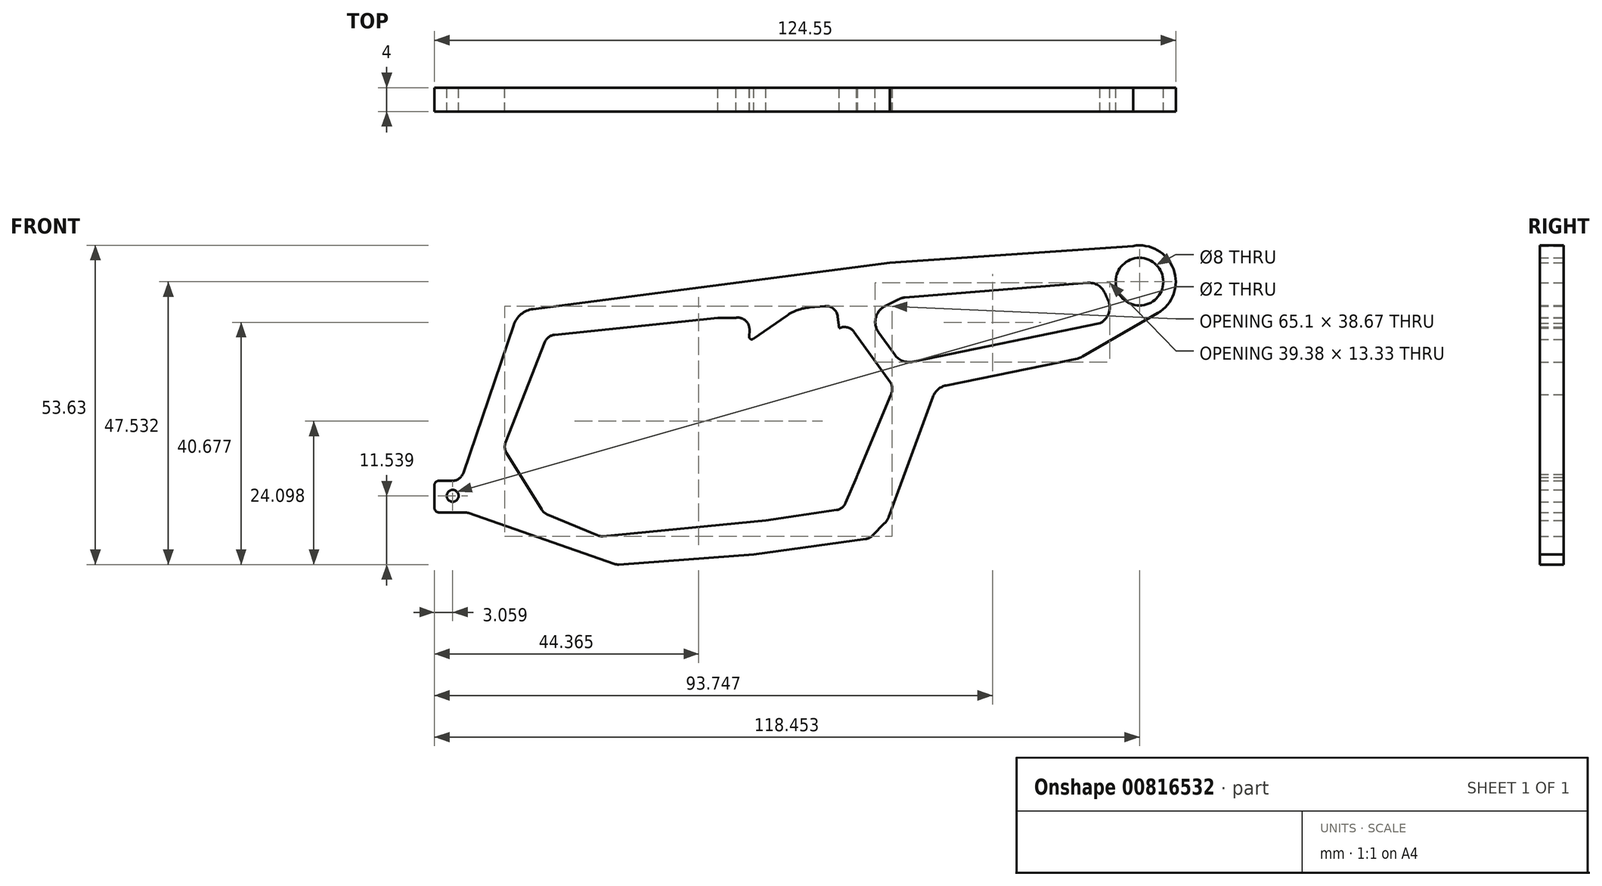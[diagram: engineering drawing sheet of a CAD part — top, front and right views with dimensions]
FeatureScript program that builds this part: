
annotation { "Feature Type Name" : "Feature", "Feature Type Description" : "" }
export const myFeature = defineFeature(function(context is Context, id is Id, definition is map)
    precondition{}
    {
        {
            assignVariable(context, id + "F0", {"name" : "GT_material", "anyValue" : 4});
        }
        {
            var Q0;
            Q0=qCreatedBy(makeId("Front.planeOp"),FACE);
            var sketch = newSketch(context, id + "F1", { "sketchPlane" : qUnion([Q0])});
            skCircle(sketch, "E0", {"center": v(51.04, 1.14) * mm, "radius": 4 * mm});
            skArc(sketch, "E1", {"start": v(-14.48, -6.96) * mm, "mid": v(-15.14, -5.41) * mm, "end": v(-16.75, -4.91) * mm});
            skLineSegment(sketch, "E2", {"start": v(-19.77, -4.91) * mm, "end": v(-16.75, -4.91) * mm});
            skLineSegment(sketch, "E3", {"start": v(-14.48, -6.96) * mm, "end": v(-14.52, -8.15) * mm});
            skLineSegment(sketch, "E4", {"start": v(-13.92, -8.48) * mm, "end": v(-8.2, -4.55) * mm});
            skLineSegment(sketch, "E5", {"start": v(49.97, 7.14) * mm, "end": v(9.1, 4.35) * mm});
            skPoint(sketch, "E6.visualSharp", {"position": v(-14.55, -8.91) * mm});
            skArc(sketch, "E6.filletArc", {"start": v(-14.52, -8.15) * mm, "mid": v(-14.32, -8.5) * mm, "end": v(-13.92, -8.48) * mm});
            skArc(sketch, "E7", {"start": v(54.1, -4.13) * mm, "mid": v(56.77, 3.24) * mm, "end": v(49.97, 7.14) * mm});
            skLineSegment(sketch, "E8", {"start": v(0.36, -4.73) * mm, "end": v(0.57, -6.68) * mm});
            skLineSegment(sketch, "E9", {"start": v(0.57, -6.68) * mm, "end": v(0.67, -6.63) * mm});
            skLineSegment(sketch, "E10", {"start": v(-1.8, -2.96) * mm, "end": v(-4.35, -3.17) * mm});
            skPoint(sketch, "E11.orphan", {"position": v(1.27, -2.7) * mm});
            skArc(sketch, "E12.filletArc", {"start": v(-4.35, -3.17) * mm, "mid": v(-6.36, -3.61) * mm, "end": v(-8.2, -4.55) * mm});
            skPoint(sketch, "E13.visualSharp", {"position": v(0.15, -2.8) * mm});
            skArc(sketch, "E14.filletArc", {"start": v(0.36, -4.73) * mm, "mid": v(-0.36, -3.4) * mm, "end": v(-1.8, -2.96) * mm});
            skArc(sketch, "E15", {"start": v(9.26, -17.84) * mm, "mid": v(9.5, -16.75) * mm, "end": v(9.13, -15.7) * mm});
            skLineSegment(sketch, "E16", {"start": v(3.1, -7.3) * mm, "end": v(9.13, -15.7) * mm});
            skArc(sketch, "E17", {"start": v(3.48, -31.72) * mm, "mid": v(3.6, -31.5) * mm, "end": v(3.67, -31.26) * mm});
            skLineSegment(sketch, "E18", {"start": v(9.42, -17.45) * mm, "end": v(3.48, -31.72) * mm});
            skLineSegment(sketch, "E19", {"start": v(4.56, -29.14) * mm, "end": v(1.69, -36.02) * mm});
            skPoint(sketch, "E19.endSnap0", {"position": v(-5.53, -33.68) * mm});
            skLineSegment(sketch, "E20", {"start": v(6.17, -41.53) * mm, "end": v(8.23, -39.46) * mm});
            skLineSegment(sketch, "E21", {"start": v(-14.63, -39.3) * mm, "end": v(-14.59, -39.4) * mm});
            skLineSegment(sketch, "E22", {"start": v(-11.75, -38.99) * mm, "end": v(0.13, -37.23) * mm});
            skPoint(sketch, "E23.visualSharp", {"position": v(1.25, -37.07) * mm});
            skArc(sketch, "E23.filletArc", {"start": v(0.13, -37.23) * mm, "mid": v(1.07, -36.83) * mm, "end": v(1.69, -36.02) * mm});
            skPoint(sketch, "E24.visualSharp", {"position": v(2.15, -6) * mm});
            skArc(sketch, "E24.filletArc", {"start": v(3.1, -7.3) * mm, "mid": v(2, -6.54) * mm, "end": v(0.67, -6.63) * mm});
            skLineSegment(sketch, "E25", {"start": v(-13.76, -44.67) * mm, "end": v(5.02, -42.11) * mm});
            skPoint(sketch, "E26.orphan", {"position": v(-5.53, -53.37) * mm});
            skLineSegment(sketch, "E27", {"start": v(9.1, 4.35) * mm, "end": v(-50.84, -3.47) * mm});
            skLineSegment(sketch, "E28", {"start": v(-19.77, -4.91) * mm, "end": v(-47.22, -7.78) * mm});
            skLineSegment(sketch, "E29", {"start": v(-11.75, -38.99) * mm, "end": v(-39.1, -41.62) * mm});
            skLineSegment(sketch, "E30", {"start": v(-36.4, -46.38) * mm, "end": v(-13.76, -44.67) * mm});
            skLineSegment(sketch, "E31", {"start": v(-48.47, -37.95) * mm, "end": v(-40.07, -41.47) * mm});
            skLineSegment(sketch, "E32", {"start": v(-64.45, -32.32) * mm, "end": v(-66.67, -32.32) * mm});
            skLineSegment(sketch, "E33", {"start": v(-66.67, -37.62) * mm, "end": v(-62.4, -37.62) * mm});
            skLineSegment(sketch, "E34", {"start": v(-61.74, -37.74) * mm, "end": v(-37.22, -46.28) * mm});
            skLineSegment(sketch, "E35", {"start": v(-48.88, -9.04) * mm, "end": v(-55.46, -25.87) * mm});
            skLineSegment(sketch, "E36", {"start": v(-55.3, -27.66) * mm, "end": v(-49.4, -37.16) * mm});
            skPoint(sketch, "E37.orphan", {"position": v(-58.53, -33.74) * mm});
            skLineSegment(sketch, "E38", {"start": v(-54.1, -6.14) * mm, "end": v(-62.56, -30.97) * mm});
            skPoint(sketch, "E39.visualSharp", {"position": v(-53.3, -3.79) * mm});
            skArc(sketch, "E39.filletArc", {"start": v(-50.84, -3.47) * mm, "mid": v(-52.85, -4.34) * mm, "end": v(-54.1, -6.14) * mm});
            skPoint(sketch, "E40.visualSharp", {"position": v(-63.02, -32.32) * mm});
            skArc(sketch, "E40.filletArc", {"start": v(-64.45, -32.32) * mm, "mid": v(-63.29, -31.95) * mm, "end": v(-62.56, -30.97) * mm});
            skPoint(sketch, "E41.visualSharp", {"position": v(-62.06, -37.62) * mm});
            skArc(sketch, "E41.filletArc", {"start": v(-61.74, -37.74) * mm, "mid": v(-62.06, -37.65) * mm, "end": v(-62.4, -37.62) * mm});
            skPoint(sketch, "E42.visualSharp", {"position": v(-36.82, -46.42) * mm});
            skArc(sketch, "E42.filletArc", {"start": v(-37.22, -46.28) * mm, "mid": v(-36.82, -46.37) * mm, "end": v(-36.4, -46.38) * mm});
            skPoint(sketch, "E43.visualSharp", {"position": v(5.7, -42.02) * mm});
            skArc(sketch, "E43.filletArc", {"start": v(5.02, -42.11) * mm, "mid": v(5.64, -41.92) * mm, "end": v(6.17, -41.53) * mm});
            skPoint(sketch, "E44.visualSharp", {"position": v(-55.82, -26.8) * mm});
            skArc(sketch, "E44.filletArc", {"start": v(-55.46, -25.87) * mm, "mid": v(-55.59, -26.78) * mm, "end": v(-55.3, -27.66) * mm});
            skPoint(sketch, "E45.visualSharp", {"position": v(-48.43, -7.9) * mm});
            skArc(sketch, "E45.filletArc", {"start": v(-47.22, -7.78) * mm, "mid": v(-48.23, -8.17) * mm, "end": v(-48.88, -9.04) * mm});
            skPoint(sketch, "E46.visualSharp", {"position": v(-49.06, -37.7) * mm});
            skArc(sketch, "E46.filletArc", {"start": v(-49.4, -37.16) * mm, "mid": v(-49, -37.62) * mm, "end": v(-48.47, -37.95) * mm});
            skPoint(sketch, "E47.visualSharp", {"position": v(-39.6, -41.67) * mm});
            skArc(sketch, "E47.filletArc", {"start": v(-40.07, -41.47) * mm, "mid": v(-39.6, -41.6) * mm, "end": v(-39.1, -41.62) * mm});
            skCircle(sketch, "E48", {"center": v(-64.35, -34.85) * mm, "radius": 1 * mm});
            skLineSegment(sketch, "E49", {"start": v(-67.41, -33.06) * mm, "end": v(-67.41, -36.88) * mm});
            skPoint(sketch, "E50.visualSharp", {"position": v(-67.41, -32.32) * mm});
            skArc(sketch, "E50.filletArc", {"start": v(-66.67, -32.32) * mm, "mid": v(-67.2, -32.54) * mm, "end": v(-67.41, -33.06) * mm});
            skPoint(sketch, "E51.visualSharp", {"position": v(-67.41, -37.62) * mm});
            skArc(sketch, "E51.filletArc", {"start": v(-67.41, -36.88) * mm, "mid": v(-67.2, -37.4) * mm, "end": v(-66.67, -37.62) * mm});
            skLineSegment(sketch, "E52", {"start": v(8.3, -2.96) * mm, "end": v(10.52, -1.83) * mm});
            skLineSegment(sketch, "E53.trimOffspring", {"start": v(7.21, -7.39) * mm, "end": v(9.9, -11.13) * mm});
            skLineSegment(sketch, "E54", {"start": v(41.48, -11.44) * mm, "end": v(54.1, -4.13) * mm});
            skArc(sketch, "E55", {"start": v(45.33, -0.99) * mm, "mid": v(45.5, -1.38) * mm, "end": v(45.68, -1.75) * mm});
            skLineSegment(sketch, "E56", {"start": v(11.63, -1.52) * mm, "end": v(42.28, 0.95) * mm});
            skPoint(sketch, "E57.visualSharp", {"position": v(44.95, 1.17) * mm});
            skArc(sketch, "E57.filletArc", {"start": v(45.33, -0.99) * mm, "mid": v(44.13, 0.5) * mm, "end": v(42.28, 0.95) * mm});
            skPoint(sketch, "E58.visualSharp", {"position": v(47.9, -4.08) * mm});
            skArc(sketch, "E58.filletArc", {"start": v(44.4, -5.85) * mm, "mid": v(45.9, -4.07) * mm, "end": v(45.68, -1.75) * mm});
            skPoint(sketch, "E59.visualSharp", {"position": v(16.33, -20.07) * mm});
            skPoint(sketch, "E60.visualSharp", {"position": v(11.05, -1.57) * mm});
            skArc(sketch, "E60.filletArc", {"start": v(11.63, -1.52) * mm, "mid": v(11.06, -1.62) * mm, "end": v(10.52, -1.83) * mm});
            skPoint(sketch, "E61.visualSharp", {"position": v(5.16, -4.54) * mm});
            skArc(sketch, "E61.filletArc", {"start": v(8.3, -2.96) * mm, "mid": v(6.73, -4.92) * mm, "end": v(7.21, -7.39) * mm});
            skLineSegment(sketch, "E62", {"start": v(44.4, -5.85) * mm, "end": v(12.94, -12.32) * mm});
            skPoint(sketch, "E63.newPointB", {"position": v(11.02, -12.72) * mm});
            skArc(sketch, "E63.filletArc", {"start": v(9.9, -11.13) * mm, "mid": v(11.25, -12.18) * mm, "end": v(12.94, -12.32) * mm});
            skLineSegment(sketch, "E64", {"start": v(40.58, -11.78) * mm, "end": v(18.56, -16.29) * mm});
            skLineSegment(sketch, "E65", {"start": v(16.35, -18.19) * mm, "end": v(8.9, -38.38) * mm});
            skArc(sketch, "E66.filletArc", {"start": v(40.58, -11.78) * mm, "mid": v(41.05, -11.65) * mm, "end": v(41.48, -11.44) * mm});
            skPoint(sketch, "E67.visualSharp", {"position": v(16.93, -16.62) * mm});
            skArc(sketch, "E67.filletArc", {"start": v(18.56, -16.29) * mm, "mid": v(17.2, -16.95) * mm, "end": v(16.35, -18.19) * mm});
            skPoint(sketch, "E68.visualSharp", {"position": v(8.68, -39) * mm});
            skArc(sketch, "E68.filletArc", {"start": v(8.23, -39.46) * mm, "mid": v(8.63, -38.96) * mm, "end": v(8.9, -38.38) * mm});
            skSolve(sketch);
        }
        {
            var Q0;
            Q0=makeQuery(id+"F1.imprint","IMPRINT",FACE,{"disambiguationData":[TD([[makeQuery(id+"F1.imprint","IMPRINT",EDGE,{"derivedFrom":sQuery(id+"F1.wireOp",EDGE,"RTn5JsXc-azhZ-ol2G-LdRP-DOtyIP9GYYN3.bottom")}),-1.0]])]});
            var Q1;
            Q1=makeQuery(id+"F1.imprint","IMPRINT",FACE,{"disambiguationData":[TD([[makeQuery(id+"F1.imprint","IMPRINT",EDGE,{"derivedFrom":sQuery(id+"F1.wireOp",EDGE,"RTn5JsXc-azhZ-ol2G-LdRP-DOtyIP9GYYN3.left")}),1.0]])]});
            var Q2;
            {var subQ4=sQuery(id+"F1.wireOp",EDGE,"kS4O2s1C-oaWE-bKg6-cGq9-rXicI0doBkGN");Q2=makeQuery(id+"F1.imprint","IMPRINT",FACE,{"disambiguationData":[TD([[makeQuery(id+"F1.imprint","IMPRINT",EDGE,{"derivedFrom":subQ4}),-1.0]])]});}
            var Q3;
            {var subQ0=sQuery(id+"F1.wireOp",EDGE,"wYxa1iAv-Rcrp-kjgY-EF02-pVXLUirzXqT7");Q3=makeQuery(id+"F1.imprint","IMPRINT",FACE,{"disambiguationData":[TD([[makeQuery(id+"F1.imprint","IMPRINT",EDGE,{"derivedFrom":subQ0}),-1.0]])]});}
            var Q4;
            {var subQ0=sQuery(id+"F1.wireOp",EDGE,"cLypqEDC-QkAd-EKEe-AvMl-Lh3HX9KfUdie");Q4=makeQuery(id+"F1.imprint","IMPRINT",FACE,{"disambiguationData":[TD([[makeQuery(id+"F1.imprint","IMPRINT",EDGE,{"derivedFrom":subQ0}),1.0]])]});}
            var Q5;
            {var subQ0=sQuery(id+"F1.wireOp",EDGE,"z8bvmrLT-e4ED-gxJd-lHsd-OczUo95YHXeM");var subQ3=sQuery(id+"F1.wireOp",EDGE,"E22");var subQ5=makeQuery(id+"F1.imprint","INTERSECT",VERTEX,{"derivedFrom":[subQ0,subQ3]});Q5=makeQuery(id+"F1.imprint","IMPRINT",FACE,{"disambiguationData":[TD([[makeQuery(id+"F1.imprint","IMPRINT",EDGE,{"disambiguationData":[TD([[subQ5,-1.0]])],"derivedFrom":subQ3}),-1.0]])]});}
            var Q6;
            Q6=makeQuery(id+"F1.imprint","IMPRINT",FACE,{"disambiguationData":[TD([[makeQuery(id+"F1.imprint","IMPRINT",EDGE,{"derivedFrom":sQuery(id+"F1.wireOp",EDGE,"E0")}),-1.0]])]});
            var Q7;
            {var subQ2=sQuery(id+"F1.wireOp",EDGE,"E28");Q7=makeQuery(id+"F1.imprint","IMPRINT",FACE,{"disambiguationData":[TD([[makeQuery(id+"F1.imprint","IMPRINT",EDGE,{"derivedFrom":subQ2}),-1.0]])]});}
            extrude(context, id + "F2", {"entities" : qUnion([Q0, Q1, Q2, Q3, Q4, Q5, Q6, Q7]), "depth" : (getVariable(context, 'GT_material')) * mm, "offsetDistance" : 25 * mm});
        }
    });
